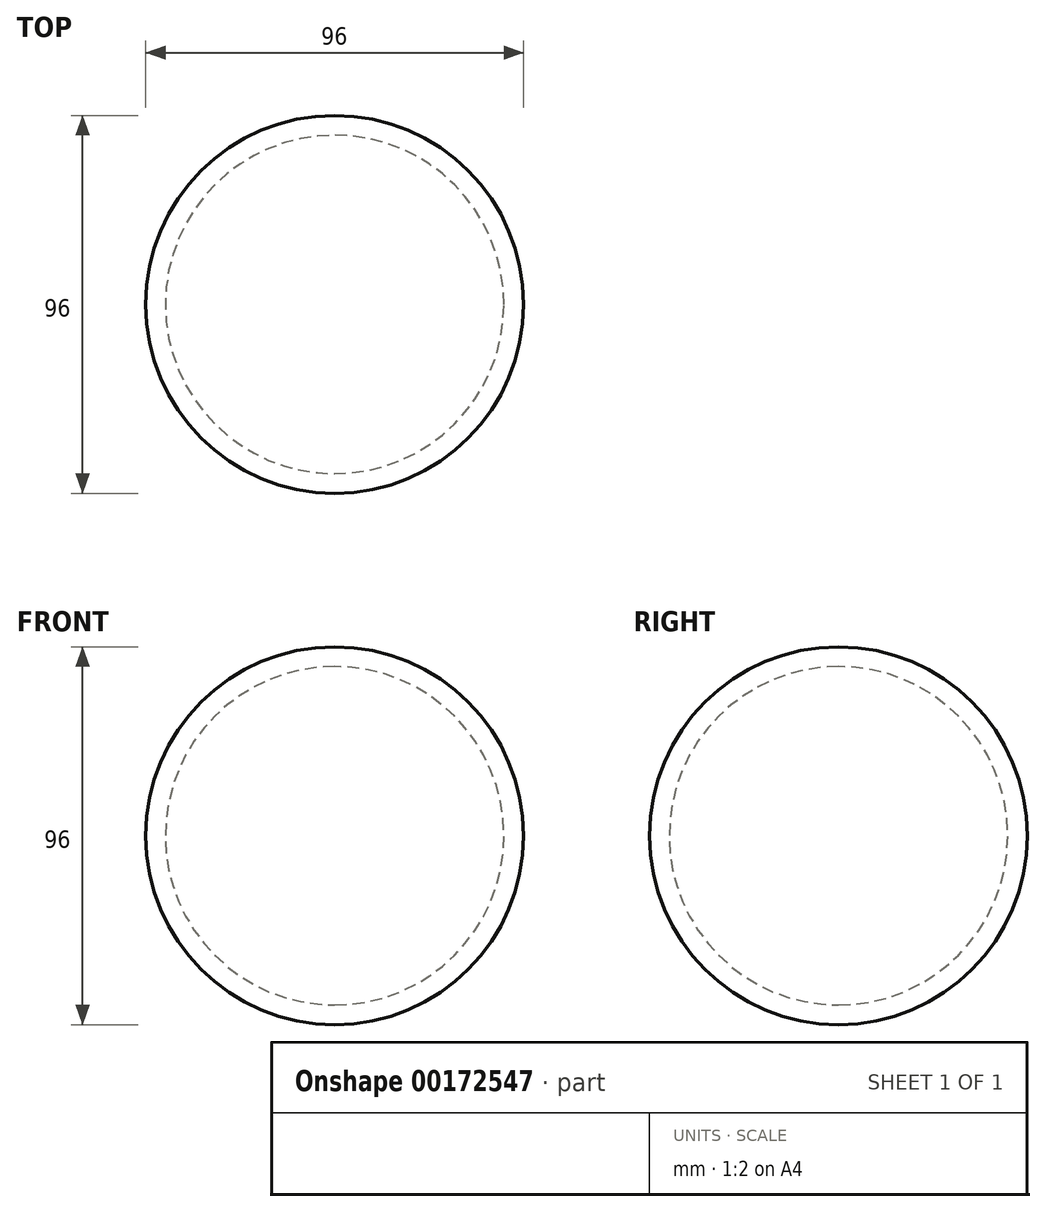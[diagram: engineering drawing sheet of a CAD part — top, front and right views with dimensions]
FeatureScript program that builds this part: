
annotation { "Feature Type Name" : "Feature", "Feature Type Description" : "" }
export const myFeature = defineFeature(function(context is Context, id is Id, definition is map)
    precondition{}
    {
        {
            var Q0;
            Q0=qCreatedBy(makeId("Front.planeOp"),FACE);
            var sketch = newSketch(context, id + "F0", { "sketchPlane" : qUnion([Q0])});
            skArc(sketch, "E0", {"start": v(0, 48) * mm, "mid": v(-48, 0) * mm, "end": v(0, -48) * mm});
            skArc(sketch, "E1", {"start": v(0, 43) * mm, "mid": v(-43, 0) * mm, "end": v(0, -43) * mm});
            skLineSegment(sketch, "E2", {"start": v(0, 48) * mm, "end": v(0, 43) * mm});
            skLineSegment(sketch, "E3.trimOffspring", {"start": v(0, -43) * mm, "end": v(0, -48) * mm});
            skSolve(sketch);
        }
        {
            var Q0;
            Q0=makeQuery(id+"F0.imprint","IMPRINT",FACE,{"disambiguationData":[TD([[makeQuery(id+"F0.imprint","IMPRINT",EDGE,{"derivedFrom":sQuery(id+"F0.wireOp",EDGE,"E0")}),1.0]])]});
            var Q1;
            Q1=sQuery(id+"F0.wireOp",EDGE,"E3.trimOffspring");
            revolve(context, id + "F1", {"entities" : qUnion([Q0]), "axis" : qUnion([Q1]), "revolveType" : RevolveType.FULL});
        }
    });
